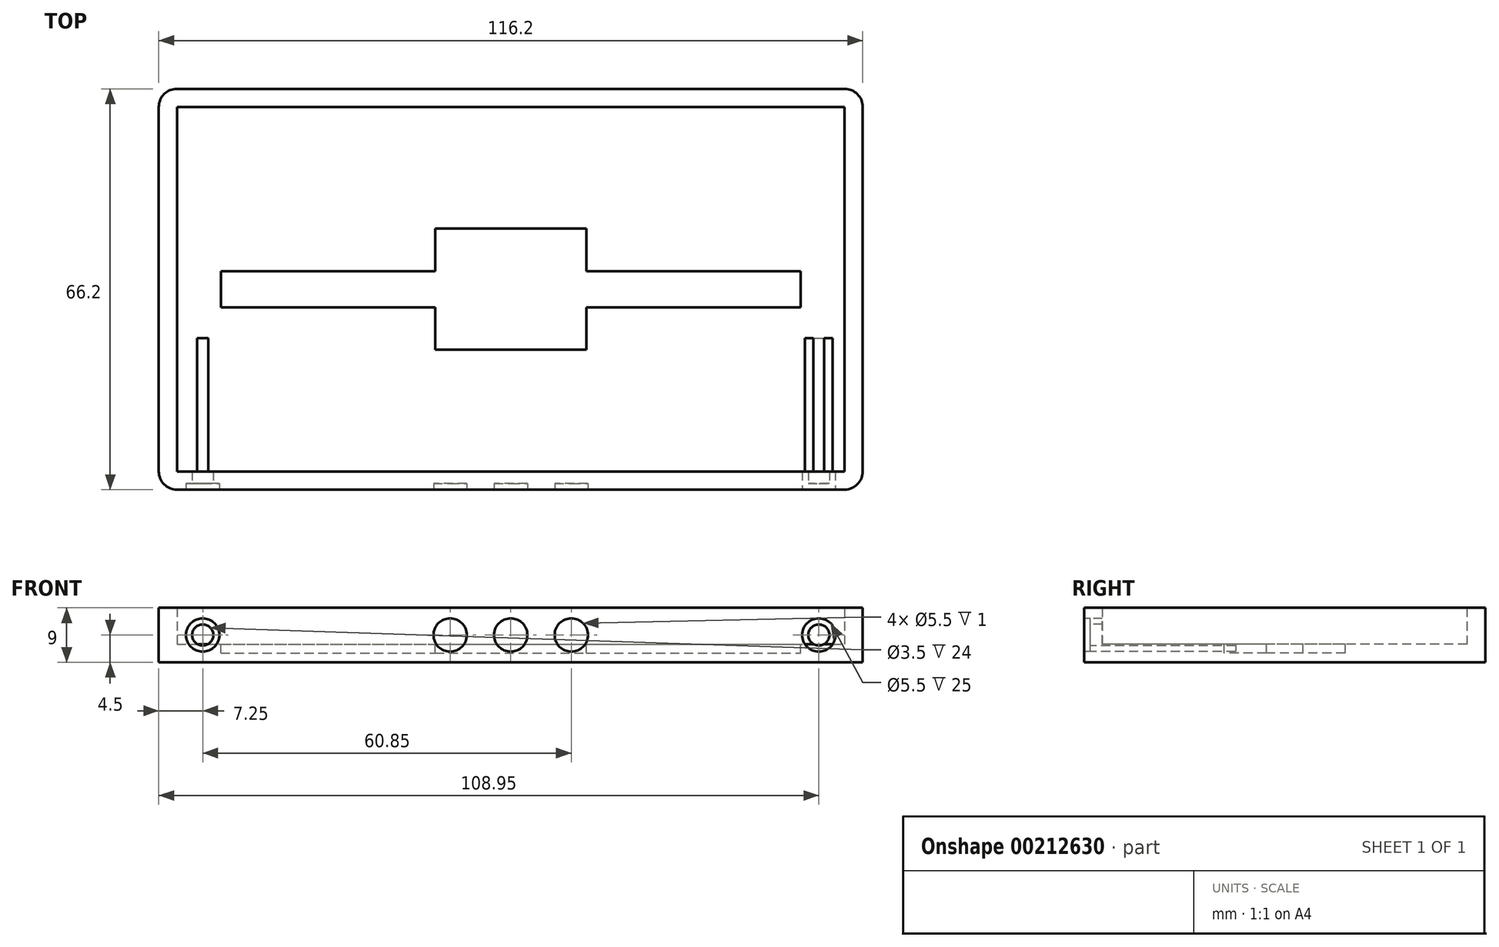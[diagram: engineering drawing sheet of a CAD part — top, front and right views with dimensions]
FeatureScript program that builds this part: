
annotation { "Feature Type Name" : "Feature", "Feature Type Description" : "" }
export const myFeature = defineFeature(function(context is Context, id is Id, definition is map)
    precondition{}
    {
        {
            var Q0;
            Q0=qCreatedBy(makeId("Top.planeOp"),FACE);
            var sketch = newSketch(context, id + "F0", { "sketchPlane" : qUnion([Q0])});
            skLineSegment(sketch, "E0.bottom", {"start": v(-55.1, 30.1) * mm, "end": v(55.1, 30.1) * mm});
            skLineSegment(sketch, "E0.top", {"start": v(-55.1, -30.1) * mm, "end": v(55.1, -30.1) * mm});
            skLineSegment(sketch, "E0.left", {"start": v(-55.1, 30.1) * mm, "end": v(-55.1, -30.1) * mm});
            skLineSegment(sketch, "E0.right", {"start": v(55.1, 30.1) * mm, "end": v(55.1, -30.1) * mm});
            skPoint(sketch, "E0.middle", {"position": v(0, 0) * mm});
            skLineSegment(sketch, "E1.0", {"start": v(-58.1, 33.1) * mm, "end": v(58.1, 33.1) * mm});
            skLineSegment(sketch, "E1.1", {"start": v(-58.1, 33.1) * mm, "end": v(-58.1, -33.1) * mm});
            skLineSegment(sketch, "E1.2", {"start": v(-58.1, -33.1) * mm, "end": v(58.1, -33.1) * mm});
            skLineSegment(sketch, "E1.3", {"start": v(58.1, 33.1) * mm, "end": v(58.1, -33.1) * mm});
            skSolve(sketch);
        }
        {
            var Q0;
            Q0=makeQuery(id+"F0.imprint","IMPRINT",FACE,{"disambiguationData":[TD([[makeQuery(id+"F0.imprint","IMPRINT",EDGE,{"derivedFrom":sQuery(id+"F0.wireOp",EDGE,"E0.bottom")}),-1.0]])]});
            extrude(context, id + "F1", {"entities" : qUnion([Q0]), "depth" : 3 * mm});
        }
        {
            var Q0;
            Q0=makeQuery(id+"F0.imprint","IMPRINT",FACE,{"disambiguationData":[TD([[makeQuery(id+"F0.imprint","IMPRINT",EDGE,{"derivedFrom":sQuery(id+"F0.wireOp",EDGE,"E0.bottom")}),1.0]])]});
            extrude(context, id + "F2", {"entities" : qUnion([Q0]), "operationType" : NewBodyOperationType.ADD, "depth" : 9 * mm});
        }
        {
            var Q0;
            Q0=makeQuery(id+"F1.opExtrude","CAP_FACE",FACE,{"disambiguationData":[OSD([sQuery(id+"F0.wireOp",EDGE,"E0.bottom"),sQuery(id+"F0.wireOp",EDGE,"E0.top"),sQuery(id+"F0.wireOp",EDGE,"E0.left"),sQuery(id+"F0.wireOp",EDGE,"E0.right")])],"isStart":false});
            var sketch = newSketch(context, id + "F3", { "sketchPlane" : qUnion([Q0])});
            skLineSegment(sketch, "E2.0.0", {"start": v(-55.1, 30.1) * mm, "end": v(-55.1, -30.1) * mm});
            skLineSegment(sketch, "E2.0.1", {"start": v(-55.1, -30.1) * mm, "end": v(55.1, -30.1) * mm});
            skLineSegment(sketch, "E2.0.2", {"start": v(55.1, -30.1) * mm, "end": v(55.1, 30.1) * mm});
            skLineSegment(sketch, "E2.0.3", {"start": v(55.1, 30.1) * mm, "end": v(-55.1, 30.1) * mm});
            skLineSegment(sketch, "E3.bottom", {"start": v(-12.5, 10) * mm, "end": v(12.5, 10) * mm});
            skLineSegment(sketch, "E3.top", {"start": v(-12.5, -10) * mm, "end": v(12.5, -10) * mm});
            skLineSegment(sketch, "E3.left", {"start": v(-12.5, 10) * mm, "end": v(-12.5, -10) * mm});
            skLineSegment(sketch, "E3.right", {"start": v(12.5, 10) * mm, "end": v(12.5, -10) * mm});
            skPoint(sketch, "E3.middle", {"position": v(0, 0) * mm});
            skLineSegment(sketch, "E4.bottom", {"start": v(-47.85, 3) * mm, "end": v(-12.5, 3) * mm});
            skLineSegment(sketch, "E4.top", {"start": v(-50.85, -3) * mm, "end": v(-12.5, -3) * mm});
            skLineSegment(sketch, "E4.left", {"start": v(-50.85, 3) * mm, "end": v(-50.85, -3) * mm});
            skLineSegment(sketch, "E4.right", {"start": v(50.85, 0) * mm, "end": v(50.85, -3) * mm});
            skLineSegment(sketch, "E5.bottom", {"start": v(-47.85, 30.1) * mm, "end": v(-53.85, 30.1) * mm});
            skLineSegment(sketch, "E5.top", {"start": v(-47.85, -30.1) * mm, "end": v(-53.85, -30.1) * mm});
            skLineSegment(sketch, "E5.left", {"start": v(-47.85, 30.1) * mm, "end": v(-47.85, -30.1) * mm});
            skLineSegment(sketch, "E5.right", {"start": v(-53.85, 30.1) * mm, "end": v(-53.85, -30.1) * mm});
            skPoint(sketch, "E5.middle", {"position": v(-50.85, 0) * mm});
            skLineSegment(sketch, "E6.bottom", {"start": v(53.85, 30.1) * mm, "end": v(47.85, 30.1) * mm});
            skLineSegment(sketch, "E6.top", {"start": v(53.85, -30.1) * mm, "end": v(47.85, -30.1) * mm});
            skLineSegment(sketch, "E6.left", {"start": v(53.85, 30.1) * mm, "end": v(53.85, -30.1) * mm});
            skLineSegment(sketch, "E6.right", {"start": v(47.85, 30.1) * mm, "end": v(47.85, -30.1) * mm});
            skPoint(sketch, "E6.middle", {"position": v(50.85, 0) * mm});
            skLineSegment(sketch, "E7.trimOffspring", {"start": v(12.5, 3) * mm, "end": v(50.85, 3) * mm});
            skLineSegment(sketch, "E8.trimOffspring", {"start": v(12.5, -3) * mm, "end": v(50.85, -3) * mm});
            skSolve(sketch);
        }
        {
            var Q0;
            {var subQ3=sQuery(id+"F3.wireOp",EDGE,"E3.bottom");Q0=makeQuery(id+"F3.imprint","IMPRINT",FACE,{"disambiguationData":[TD([[makeQuery(id+"F3.imprint","IMPRINT",EDGE,{"derivedFrom":subQ3}),-1.0]])]});}
            var Q1;
            {var subQ0=sQuery(id+"F3.wireOp",EDGE,"E4.bottom");Q1=makeQuery(id+"F3.imprint","IMPRINT",FACE,{"disambiguationData":[TD([[makeQuery(id+"F3.imprint","IMPRINT",EDGE,{"derivedFrom":subQ0}),-1.0]])]});}
            var Q2;
            {var subQ0=sQuery(id+"F3.wireOp",EDGE,"E7.trimOffspring");var subQ1=sQuery(id+"F3.wireOp",EDGE,"E3.right");var subQ2=makeQuery(id+"F3.imprint","INTERSECT",VERTEX,{"derivedFrom":[subQ1,subQ0]});Q2=makeQuery(id+"F3.imprint","IMPRINT",FACE,{"disambiguationData":[TD([[makeQuery(id+"F3.imprint","IMPRINT",EDGE,{"disambiguationData":[TD([[subQ2,-1.0]])],"derivedFrom":subQ1}),1.0]])]});}
            var Q3;
            {var subQ3=sQuery(id+"F3.wireOp",EDGE,"E5.bottom");Q3=makeQuery(id+"F3.imprint","IMPRINT",FACE,{"disambiguationData":[TD([[makeQuery(id+"F3.imprint","IMPRINT",EDGE,{"derivedFrom":subQ3}),-1.0]])]});}
            var Q4;
            {var subQ1=sQuery(id+"F3.wireOp",EDGE,"E6.bottom");Q4=makeQuery(id+"F3.imprint","IMPRINT",FACE,{"disambiguationData":[TD([[makeQuery(id+"F3.imprint","IMPRINT",EDGE,{"derivedFrom":subQ1}),-1.0]])]});}
            extrude(context, id + "F4", {"entities" : qUnion([Q0, Q1, Q2, Q3, Q4]), "operationType" : NewBodyOperationType.REMOVE, "oppositeDirection" : true, "depth" : 1.5 * mm});
        }
        {
            var Q0;
            Q0=makeQuery(id+"F2.opExtrude","SWEPT_FACE",FACE,{"disambiguationData":[OSD([sQuery(id+"F0.wireOp",EDGE,"E1.2")])]});
            var sketch = newSketch(context, id + "F5", { "sketchPlane" : qUnion([Q0])});
            skCircle(sketch, "E9", {"center": v(-50.85, 4.5) * mm, "radius": 2.75 * mm});
            skCircle(sketch, "E10", {"center": v(-50.85, 4.5) * mm, "radius": 1.75 * mm});
            skLineSegment(sketch, "E11", {"start": v(0, 9) * mm, "end": v(0, 0) * mm, "construction": true});
            skCircle(sketch, "E12.MirrorC", {"center": v(50.85, 4.5) * mm, "radius": 1.75 * mm});
            skCircle(sketch, "E13.MirrorC", {"center": v(50.85, 4.5) * mm, "radius": 2.75 * mm});
            skPoint(sketch, "E14", {"position": v(-58.1, 4.5) * mm});
            skCircle(sketch, "E15", {"center": v(0, 4.5) * mm, "radius": 2.75 * mm});
            skCircle(sketch, "E16", {"center": v(-10, 4.5) * mm, "radius": 2.75 * mm});
            skCircle(sketch, "E17", {"center": v(10, 4.5) * mm, "radius": 2.75 * mm});
            skSolve(sketch);
        }
        {
            var Q0;
            Q0=makeQuery(id+"F5.imprint","IMPRINT",FACE,{"disambiguationData":[TD([[makeQuery(id+"F5.imprint","IMPRINT",EDGE,{"derivedFrom":sQuery(id+"F5.wireOp",EDGE,"E10")}),1.0]])]});
            var Q1;
            Q1=makeQuery(id+"F5.imprint","IMPRINT",FACE,{"disambiguationData":[TD([[makeQuery(id+"F5.imprint","IMPRINT",EDGE,{"derivedFrom":sQuery(id+"F5.wireOp",EDGE,"E12.MirrorC")}),-1.0]])]});
            extrude(context, id + "F6", {"entities" : qUnion([Q0, Q1]), "operationType" : NewBodyOperationType.REMOVE, "oppositeDirection" : true, "depth" : 25 * mm});
        }
        {
            var Q0;
            Q0=makeQuery(id+"F5.imprint","IMPRINT",FACE,{"disambiguationData":[TD([[makeQuery(id+"F5.imprint","IMPRINT",EDGE,{"derivedFrom":sQuery(id+"F5.wireOp",EDGE,"E9")}),1.0]])]});
            var Q1;
            Q1=makeQuery(id+"F5.imprint","IMPRINT",FACE,{"disambiguationData":[TD([[makeQuery(id+"F5.imprint","IMPRINT",EDGE,{"derivedFrom":sQuery(id+"F5.wireOp",EDGE,"E16")}),1.0]])]});
            var Q2;
            Q2=makeQuery(id+"F5.imprint","IMPRINT",FACE,{"disambiguationData":[TD([[makeQuery(id+"F5.imprint","IMPRINT",EDGE,{"derivedFrom":sQuery(id+"F5.wireOp",EDGE,"E15")}),1.0]])]});
            var Q3;
            Q3=makeQuery(id+"F5.imprint","IMPRINT",FACE,{"disambiguationData":[TD([[makeQuery(id+"F5.imprint","IMPRINT",EDGE,{"derivedFrom":sQuery(id+"F5.wireOp",EDGE,"E17")}),1.0]])]});
            var Q4;
            Q4=makeQuery(id+"F5.imprint","IMPRINT",FACE,{"disambiguationData":[TD([[makeQuery(id+"F5.imprint","IMPRINT",EDGE,{"derivedFrom":sQuery(id+"F5.wireOp",EDGE,"E12.MirrorC")}),1.0]])]});
            extrude(context, id + "F7", {"entities" : qUnion([Q0, Q1, Q2, Q3, Q4]), "operationType" : NewBodyOperationType.REMOVE, "oppositeDirection" : true, "depth" : 1 * mm});
        }
        {
            var Q0;
            Q0=makeQuery(id+"F2.opExtrude","SWEPT_EDGE",EDGE,{"disambiguationData":[OSD([sQuery(id+"F0.wireOp",EDGE,"E1.2"),sQuery(id+"F0.wireOp",EDGE,"E1.3")])]});
            var Q1;
            Q1=makeQuery(id+"F2.opExtrude","SWEPT_EDGE",EDGE,{"disambiguationData":[OSD([sQuery(id+"F0.wireOp",EDGE,"E1.1"),sQuery(id+"F0.wireOp",EDGE,"E1.2")])]});
            var Q2;
            Q2=makeQuery(id+"F2.opExtrude","SWEPT_EDGE",EDGE,{"disambiguationData":[OSD([sQuery(id+"F0.wireOp",EDGE,"E1.0"),sQuery(id+"F0.wireOp",EDGE,"E1.3")])]});
            var Q3;
            Q3=makeQuery(id+"F2.opExtrude","SWEPT_EDGE",EDGE,{"disambiguationData":[OSD([sQuery(id+"F0.wireOp",EDGE,"E1.0"),sQuery(id+"F0.wireOp",EDGE,"E1.1")])]});
            fillet(context, id + "F8", {"entities" : qUnion([Q0, Q1, Q2, Q3]), "radius" : 3 * mm, "tangentPropagation" : true, "allowEdgeOverflow" : false});
        }
    });
